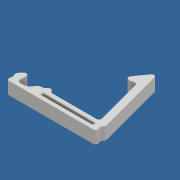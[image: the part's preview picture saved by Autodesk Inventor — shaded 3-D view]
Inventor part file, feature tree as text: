
AUTODESK INVENTOR PART (.ipt)
format: ipt  version: 2017 (Build 210142000, 142)  size: 436,736 bytes
history: native  units: mm
features: extrude x4, fillet x4, sketch x4, other x3, projected_geometry x1
ambient origin geometry x8: Origin, YZ Plane, XZ Plane, XY Plane, X Axis, Y Axis, Z Axis, Center Point
bodies: Body1 (feature_tree)
feature tree (16):
  other  "ソリッド1"
  extrude  "押し出し1"  Depth=50.0mm
  extrude  "押し出し2"  Depth=13.0mm
  extrude  "押し出し3"  Depth=7.5mm
  fillet  "フィレット1"  Radius=10.0mm
  fillet  "フィレット2"  Radius=5.0mm
  fillet  "フィレット3"  Radius=8.0mm
  other  "smaho_mount:1"
  extrude  "押し出し4"  Depth=7.8mm
  fillet  "フィレット4"  Radius=75.0mm
  sketch  "スケッチ1"
  sketch  "スケッチ2"
  sketch  "スケッチ3"
  sketch  "スケッチ5"
  projected_geometry  "投影ループ1"
  other  "メッシュ フィーチャ2"
